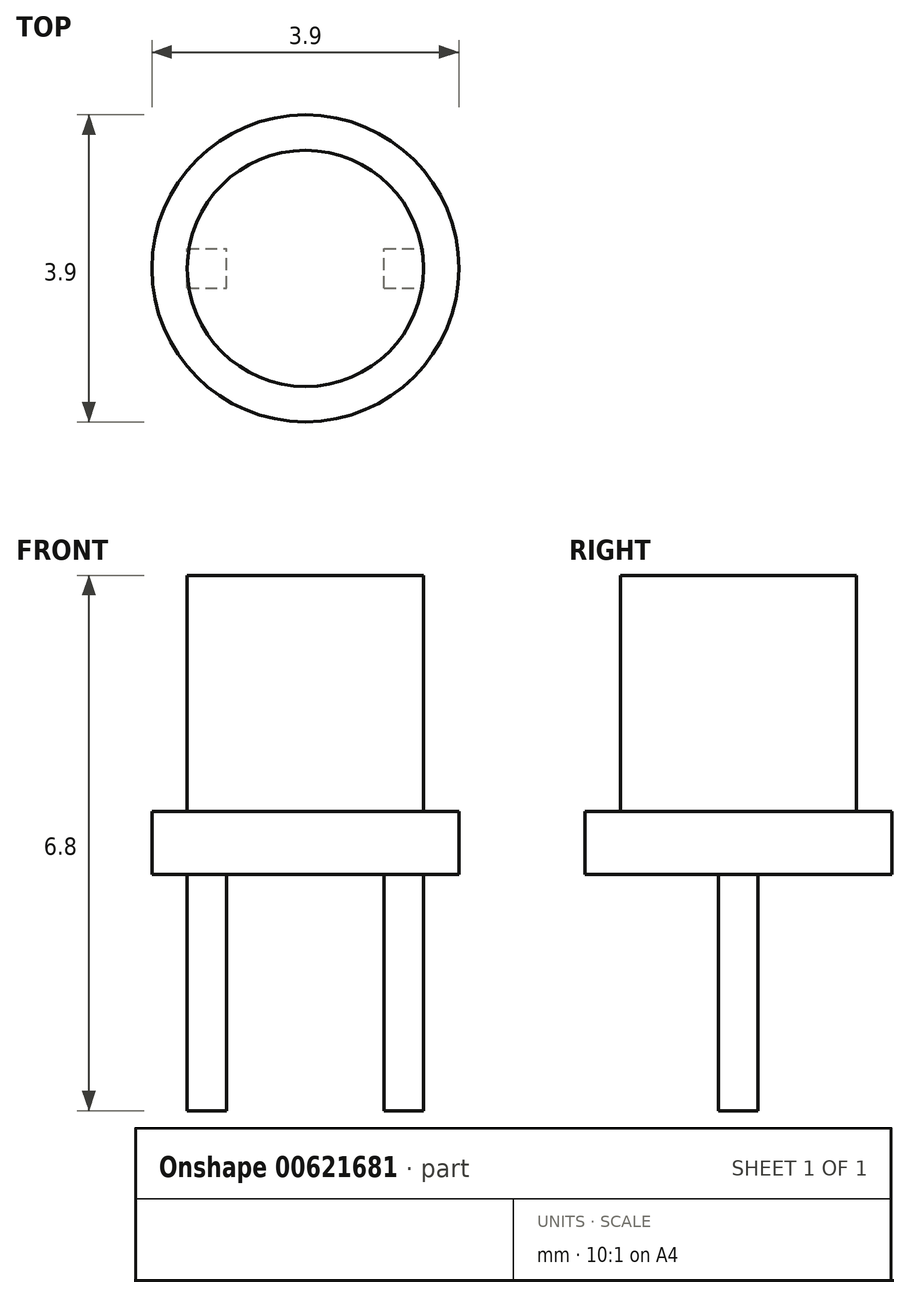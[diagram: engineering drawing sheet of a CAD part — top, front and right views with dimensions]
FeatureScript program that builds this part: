
annotation { "Feature Type Name" : "Feature", "Feature Type Description" : "" }
export const myFeature = defineFeature(function(context is Context, id is Id, definition is map)
    precondition{}
    {
        {
            var Q0;
            Q0=qCreatedBy(makeId("Top.planeOp"),FACE);
            var sketch = newSketch(context, id + "F0", { "sketchPlane" : qUnion([Q0])});
            skCircle(sketch, "E0", {"center": v(0, 0) * mm, "radius": 1.95 * mm});
            skSolve(sketch);
        }
        {
            var Q0;
            Q0=qSketchRegion(id+"F0",true);
            extrude(context, id + "F1", {"entities" : qUnion([Q0]), "depth" : .8 * mm});
        }
        {
            var Q0;
            Q0=makeQuery(id+"F1.opExtrude","CAP_FACE",FACE,{"disambiguationData":[OSD([sQuery(id+"F0.wireOp",EDGE,"E0")])],"isStart":false});
            var sketch = newSketch(context, id + "F2", { "sketchPlane" : qUnion([Q0])});
            skCircle(sketch, "E1", {"center": v(0, 0) * mm, "radius": 1.5 * mm});
            skSolve(sketch);
        }
        {
            var Q0;
            Q0=qSketchRegion(id+"F2",true);
            extrude(context, id + "F3", {"entities" : qUnion([Q0]), "operationType" : NewBodyOperationType.ADD, "depth" : 3 * mm, "offsetDistance" : 25 * mm});
        }
        {
            var Q0;
            Q0=qCreatedBy(makeId("Front.planeOp"),FACE);
            var sketch = newSketch(context, id + "F4", { "sketchPlane" : qUnion([Q0])});
            skLineSegment(sketch, "E2", {"start": v(0, -0.9) * mm, "end": v(0, -7.84) * mm, "construction": true});
            skLineSegment(sketch, "E3", {"start": v(-1.25, -0.9) * mm, "end": v(-1.25, -7.96) * mm});
            skLineSegment(sketch, "E4", {"start": v(1.25, -0.97) * mm, "end": v(1.25, -7.53) * mm});
            skLineSegment(sketch, "E5.0", {"start": v(1, 0.17) * mm, "end": v(1, -3) * mm});
            skLineSegment(sketch, "E6.0", {"start": v(1.5, 0.17) * mm, "end": v(1.5, -3) * mm});
            skLineSegment(sketch, "E7.0", {"start": v(-0.25, -0.33) * mm, "end": v(-0.25, -7.84) * mm});
            skLineSegment(sketch, "E8.0", {"start": v(0.25, -0.33) * mm, "end": v(0.25, -7.84) * mm});
            skLineSegment(sketch, "E9.0", {"start": v(-1, 0.07) * mm, "end": v(-1, -7.96) * mm});
            skLineSegment(sketch, "E10.0", {"start": v(-1.5, 0.07) * mm, "end": v(-1.5, -7.96) * mm});
            skLineSegment(sketch, "E11", {"start": v(1.5, -3) * mm, "end": v(1, -3) * mm});
            skLineSegment(sketch, "E12.trimOffspring", {"start": v(-1, -3) * mm, "end": v(-1.5, -3) * mm});
            skLineSegment(sketch, "E13.trimOffspring", {"start": v(0.25, -3) * mm, "end": v(-0.25, -3) * mm, "construction": true});
            skLineSegment(sketch, "E14", {"start": v(-1.5, 0.07) * mm, "end": v(-1, 0.07) * mm});
            skLineSegment(sketch, "E15", {"start": v(1, 0.17) * mm, "end": v(1.5, 0.17) * mm});
            skSolve(sketch);
        }
        {
            var Q0;
            Q0=qSketchRegion(id+"F4",true);
            extrude(context, id + "F5", {"entities" : qUnion([Q0]), "operationType" : NewBodyOperationType.ADD, "depth" : .25 * mm, "hasSecondDirection" : true, "secondDirectionOppositeDirection" : true, "secondDirectionDepth" : .25 * mm});
        }
    });
